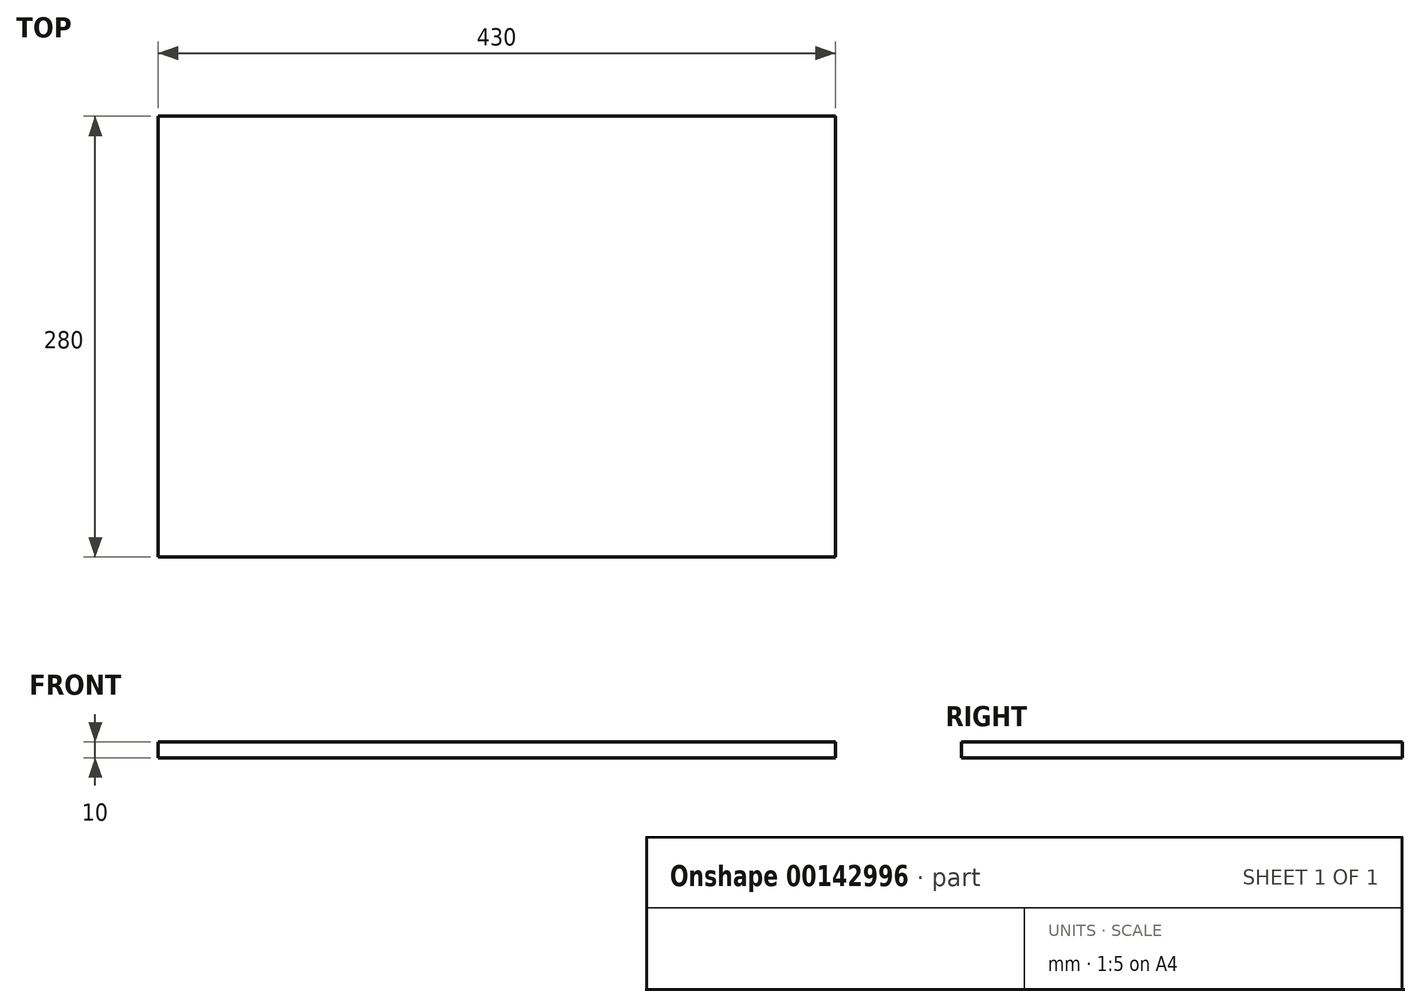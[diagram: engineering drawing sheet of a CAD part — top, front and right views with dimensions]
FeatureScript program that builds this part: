
annotation { "Feature Type Name" : "Feature", "Feature Type Description" : "" }
export const myFeature = defineFeature(function(context is Context, id is Id, definition is map)
    precondition{}
    {
        {
            var Q0;
            Q0=qCreatedBy(makeId("Top.planeOp"),FACE);
            var sketch = newSketch(context, id + "F0", { "sketchPlane" : qUnion([Q0])});
            skLineSegment(sketch, "E0.bottom", {"start": v(0, 0) * mm, "end": v(430, 0) * mm});
            skLineSegment(sketch, "E0.top", {"start": v(0, 280) * mm, "end": v(430, 280) * mm});
            skLineSegment(sketch, "E0.left", {"start": v(0, 0) * mm, "end": v(0, 280) * mm});
            skLineSegment(sketch, "E0.right", {"start": v(430, 0) * mm, "end": v(430, 280) * mm});
            skSolve(sketch);
        }
        {
            var Q0;
            Q0 = qSketchRegion(id + "F0", true);
            extrude(context, id + "F1", {"entities" : qUnion([Q0]), "depth" : 10 * mm, "offsetDistance" : 25 * mm});
        }
    });
